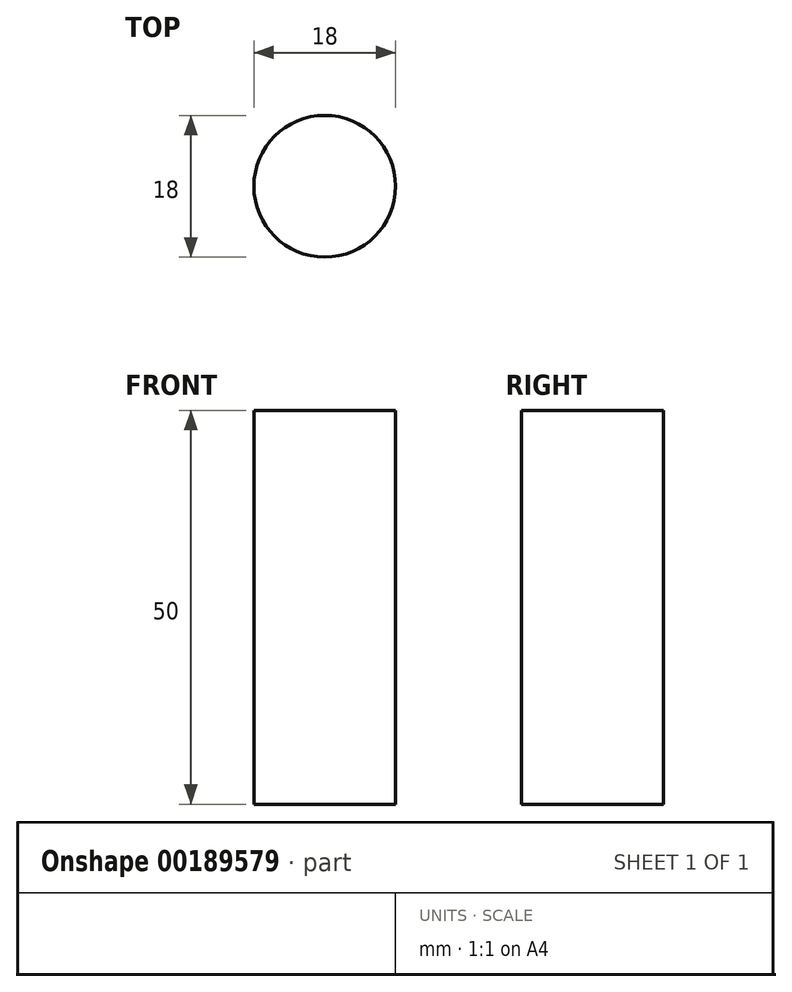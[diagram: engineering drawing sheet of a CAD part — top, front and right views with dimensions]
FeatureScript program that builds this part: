
annotation { "Feature Type Name" : "Feature", "Feature Type Description" : "" }
export const myFeature = defineFeature(function(context is Context, id is Id, definition is map)
    precondition{}
    {
        {
            var Q0;
            Q0=qCreatedBy(makeId("Top.planeOp"),FACE);
            var sketch = newSketch(context, id + "F0", { "sketchPlane" : qUnion([Q0])});
            skCircle(sketch, "E0", {"center": v(0, 0) * mm, "radius": 9 * mm});
            skSolve(sketch);
        }
        {
            var Q0;
            Q0=makeQuery(id+"F0.imprint","IMPRINT",FACE,{"disambiguationData":[TD([[makeQuery(id+"F0.imprint","IMPRINT",EDGE,{"derivedFrom":sQuery(id+"F0.wireOp",EDGE,"E0")}),1.0]])]});
            extrude(context, id + "F1", {"entities" : qUnion([Q0]), "endBound" : BoundingType.SYMMETRIC, "depth" : 50 * mm});
        }
    });
